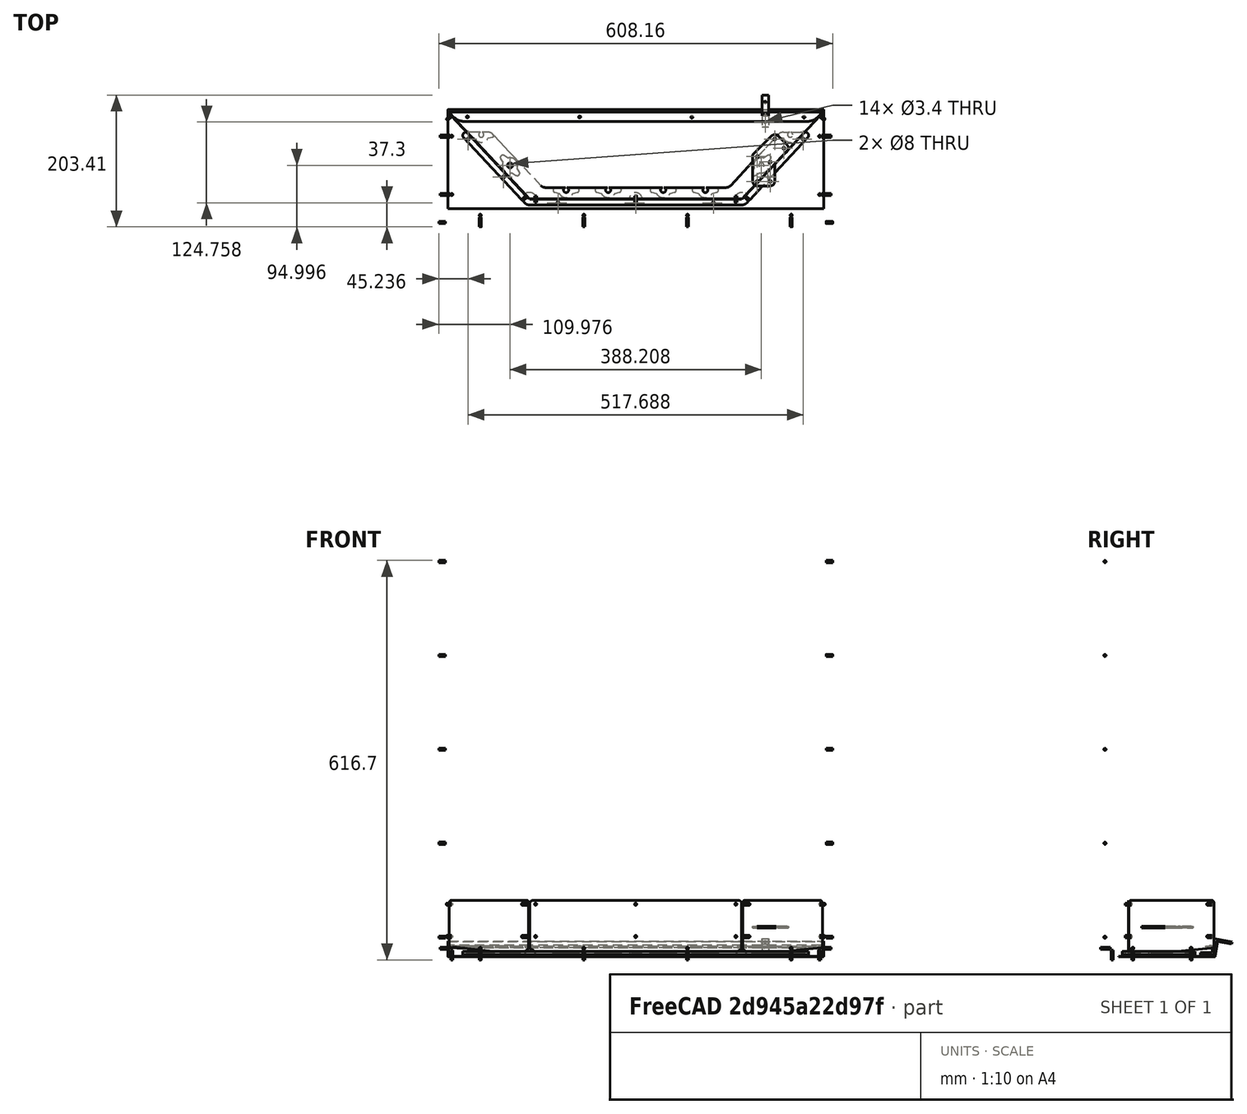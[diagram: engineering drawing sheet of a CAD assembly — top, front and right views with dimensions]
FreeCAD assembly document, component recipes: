
FREECAD ASSEMBLY — COMPONENT RECIPES ("composit_stand5")

This assembly document has 19 components, labeled P0..P18 below (a component is one placed body or linked part). 18 of them carry a construction recipe — the FreeCAD feature program that regenerates the part from scratch, quoted from this document or its linked companion documents; the rest are supplied as boundary geometry only. No exploded tour is included for this assembly.
NOTE — document 2 of 2 of this assembly tour. The two overview renders and the header above are repeated from document 1; the component sections below continue where the previous document stopped.
COMPONENT P18 — recipe-attached ("top", modeled in this document).
Construction recipe (the document's own serialized feature program — sketch geometry with constraints, then the solid features built on it; lengths are millimeters unless a unit is written):

FEATURE [PartDesign::SubShapeBinder] Binder006
  BindCopyOnChange = 0
  BindMode = 0
  ClaimChildren = true
  Context = -> Body002 [Binder006.]
  Fuse = false
  MakeFace = true
  OffsetFill = false
  OffsetIntersection = false
  OffsetJoinType = 0
  OffsetOpenResult = false
  PartialLoad = false
  Relative = false
  Support = -> [Compound006]
  _Version = 2
FEATURE [PartDesign::Pad] Pad
  Direction = (0,0,1)
  Length = 5
  Length2 = 10
  Profile = -> Binder006
  Type = 0
FEATURE [PartDesign::SubShapeBinder] Binder007
  BindCopyOnChange = 0
  BindMode = 0
  ClaimChildren = true
  Context = -> Body002 [Binder007.]
  Fuse = false
  MakeFace = true
  OffsetFill = false
  OffsetIntersection = false
  OffsetJoinType = 0
  OffsetOpenResult = false
  PartialLoad = false
  Relative = false
  Support = -> [Populate008]
  _Version = 2
FEATURE [PartDesign::Pocket] Pocket005
  BaseFeature = -> Pad
  Direction = (0,0,-1)
  Length = 2.5
  Length2 = 5
  Profile = -> Binder007
  Reversed = true
  Type = 0
FEATURE [PartDesign::SubShapeBinder] Binder008
  BindCopyOnChange = 0
  BindMode = 0
  ClaimChildren = true
  Context = -> Body002 [Binder008.]
  Fuse = false
  MakeFace = true
  OffsetFill = false
  OffsetIntersection = false
  OffsetJoinType = 0
  OffsetOpenResult = false
  PartialLoad = false
  Relative = false
  Support = -> [Populate010]
  _Version = 2
FEATURE [PartDesign::Pocket] Pocket006
  BaseFeature = -> Pocket005
  Direction = (0,0,-1)
  Length = 5
  Length2 = 5
  Midplane = true
  Profile = -> Binder008
  Type = 1
FEATURE [PartDesign::SubShapeBinder] Binder010
  BindCopyOnChange = 0
  BindMode = 0
  ClaimChildren = true
  Context = -> Body003 [Binder010.]
  Fuse = false
  MakeFace = true
  OffsetFill = false
  OffsetIntersection = false
  OffsetJoinType = 0
  OffsetOpenResult = false
  PartialLoad = false
  Relative = false
  Support = -> [Populate009]
  _Version = 2
FEATURE [PartDesign::SubShapeBinder] Binder012
  BindCopyOnChange = 0
  BindMode = 0
  ClaimChildren = true
  Context = -> Part002 [Body003.Binder012.]
  Fuse = false
  MakeFace = true
  OffsetFill = false
  OffsetIntersection = false
  OffsetJoinType = 0
  OffsetOpenResult = false
  PartialLoad = false
  Relative = true
  Support = -> [Body[Pocket008.Sketch013.]]
  _Version = 2
FEATURE [PartDesign::SubShapeBinder] Binder013
  BindCopyOnChange = 0
  BindMode = 0
  ClaimChildren = false
  Context = -> Part002 [Body002.Binder013.]
  Fuse = false
  MakeFace = true
  OffsetFill = false
  OffsetIntersection = false
  OffsetJoinType = 0
  OffsetOpenResult = false
  PartialLoad = false
  Relative = true
  Support = -> [Body[Pocket008.Sketch013.]]
  _Version = 2
FEATURE [PartDesign::Pocket] Pocket010
  BaseFeature = -> Pocket006
  Direction = (0,0,-1)
  Length = 5
  Length2 = 5
  Midplane = true
  Profile = -> Binder013
  Type = 1
FEATURE [Sketcher::SketchObject] Sketch027
  FullyConstrained = true
  MapMode = 5
  Support = -> [XY_Plane003]
FEATURE [Sketcher::SketchObject] Sketch029
  FullyConstrained = true
  MapMode = 5
  Placement = pos=(0,0,0) rot=(1,0,0;1.5708rad)
  Support = -> [XZ_Plane003]
FEATURE [PartDesign::SubShapeBinder] Binder022
  BindCopyOnChange = 0
  BindMode = 0
  ClaimChildren = true
  Fuse = false
  MakeFace = true
  OffsetFill = false
  OffsetIntersection = false
  OffsetJoinType = 0
  OffsetOpenResult = false
  PartialLoad = false
  Relative = false
  Support = -> [Populate013]
  _Version = 2
FEATURE [PartDesign::Pocket] Pocket030
  BaseFeature = -> Pocket010
  Direction = (0,0,-1)
  Length = 1
  Length2 = 5
  Profile = -> Binder022
  Reversed = true
  Type = 0
FEATURE [PartDesign::Body] Body002  label="droppers_top_fix"
  Group = -> [Binder006,Pad,Binder007,Pocket005,Binder008,Pocket006,Binder013,Pocket010,Binder022,Pocket030]
  Origin = -> Origin002
  Placement = pos=(0,0,3) rot=(0,0,1;0rad)
  Tip = -> Pocket030
FEATURE [Sketcher::SketchObject] Sketch043
  AttachmentOffset = pos=(0,0,290) rot=(0,0,1;0rad)
  FullyConstrained = true
  MapMode = 5
  Placement = pos=(290,0,0) rot=(0.57735,0.57735,0.57735;2.0944rad)
  Support = -> [YZ_Plane003]
  expr: Constraints[10] = <<main_sketch>>.Constraints.length
  sketch-geometry (5):
    g0: LineSegment StartX=124.058 StartY=0 StartZ=0 EndX=164.058 EndY=0 EndZ=0
    g1: LineSegment StartX=164.058 StartY=0 StartZ=0 EndX=164.058 EndY=30 EndZ=0
    g2: LineSegment StartX=164.058 StartY=30 StartZ=0 EndX=124.058 EndY=30 EndZ=0
    g3: LineSegment StartX=124.058 StartY=30 StartZ=0 EndX=124.058 EndY=0 EndZ=0
    g4: GeomPoint X=134.058 Y=0 Z=0
  constraints (14):
    c: Coincident(g0,g1)
    c: Coincident(g1,g2)
    c: Coincident(g2,g3)
    c: Coincident(g3,g0)
    c: Horizontal(g0)
    c: Horizontal(g2)
    c: Vertical(g1)
    c: Vertical(g3)
    c: PointOnObject(g0,g-1)
    c: PointOnObject(g4,g-1)
    c: DistanceX(g4) = 134.058
    c: DistanceX(g0,g4) = 10
    c: DistanceY(g0,g2) = 30
    c: DistanceX(g0,g0) = 40
FEATURE [PartDesign::SubShapeBinder] Binder023
  BindCopyOnChange = 0
  BindMode = 0
  ClaimChildren = false
  Context = -> Part002 [Body012.Binder023.]
  Fuse = false
  MakeFace = true
  OffsetFill = false
  OffsetIntersection = false
  OffsetJoinType = 0
  OffsetOpenResult = false
  PartialLoad = false
  Relative = true
  Support = -> [Body003[Pocket021.Sketch026.]]
  _Version = 2
FEATURE [Sketcher::SketchObject] Sketch044
  ExternalGeometry = -> [Binder023]
  FullyConstrained = true
  MapMode = 5
  Support = -> [XY_Plane015]
  sketch-geometry (5):
    g0: LineSegment StartX=175.913 StartY=-11.05 StartZ=0 EndX=289.858 EndY=110.695 EndZ=0
    g1: LineSegment StartX=289.858 StartY=110.695 StartZ=0 EndX=297.084 EndY=110.695 EndZ=0
    g2: LineSegment StartX=297.084 StartY=110.695 StartZ=0 EndX=297.084 EndY=-11.05 EndZ=0
    g3: LineSegment StartX=175.913 StartY=-11.05 StartZ=0 EndX=297.084 EndY=-11.05 EndZ=0
    g4: LineSegment StartX=289.858 StartY=110.695 StartZ=0 EndX=289.274 EndY=111.242 EndZ=0
  constraints (14):
    c: Coincident(g1,g0)
    c: Horizontal(g1)
    c: Coincident(g2,g1)
    c: Vertical(g2)
    c: Coincident(g3,g0)
    c: Coincident(g3,g2)
    c: Horizontal(g3)
    c: Coincident(g4,g0)
    c: Coincident(g4,g-3)
    c: Perpendicular(g-3,g4)
    c: Perpendicular(g0,g4)
    c: Distance(g4) = 0.8
    c: Horizontal(g-3,g0)
    c: Distance(g1,g-4) = 3
FEATURE [PartDesign::FeaturePython] BaseBend007  # WARN: FeaturePython — macro-defined, semantics opaque (R4)
  BendSide = 0
  BendSketch = -> Sketch044
  MidPlane = false
  Reverse = false
  length = 100
  radius = 0.1
  thickness = 0.3
  expr: radius = composit_properties#<<Properties>>.bend_r
  expr: thickness = composit_properties#<<Properties>>.al_thickness
FEATURE [PartDesign::FeaturePython] Bend  # WARN: FeaturePython — macro-defined, semantics opaque (R4)
  AutoMiter = true
  BaseFeature = -> BaseBend007
  BendType = 0
  LengthList = [20]
  LengthSpec = 0
  ReliefFactor = 0.7
  UseReliefFactor = false
  angle = 90
  baseObject = -> BaseBend007 [Edge3]
  bendAList = [90]
  extend1 = 0
  extend2 = 0
  gap1 = 0
  gap2 = 0
  invert = false
  kfactor = 0.5
  length = 20
  maxExtendDist = 5
  minGap = 0.1
  minReliefGap = 1
  miterangle1 = 0
  miterangle2 = 0
  offset = 0
  radius = 0.1
  reliefType = 0
  reliefd = 1
  reliefw = 0.8
  sketchflip = false
  sketchinvert = false
  unfold = false
  expr: radius = BaseBend.radius
FEATURE [PartDesign::SubShapeBinder] Binder024
  BindCopyOnChange = 0
  BindMode = 0
  ClaimChildren = true
  Context = -> Part002 [Body012.Binder024.]
  Fuse = false
  MakeFace = true
  OffsetFill = false
  OffsetIntersection = false
  OffsetJoinType = 0
  OffsetOpenResult = false
  PartialLoad = false
  Relative = true
  Support = -> [Body003[Pocket031.Sketch045.]]
  _Version = 2
FEATURE [PartDesign::Pocket] Pocket032
  BaseFeature = -> Bend
  Direction = (-0.730107,0.683333,-2.3e-15)
  Length = 5
  Length2 = 5
  Profile = -> Binder024
  Reversed = true
  Type = 0
FEATURE [PartDesign::SubShapeBinder] Binder025
  BindCopyOnChange = 0
  BindMode = 0
  ClaimChildren = false
  Context = -> Part002 [Body012.Binder025.]
  Fuse = false
  MakeFace = true
  OffsetFill = false
  OffsetIntersection = false
  OffsetJoinType = 0
  OffsetOpenResult = false
  PartialLoad = false
  Relative = true
  Support = -> [Body[Sketch013.]]
  _Version = 2
FEATURE [PartDesign::Pocket] Pocket033
  BaseFeature = -> Pocket032
  Direction = (0,0,-1)
  Length = 5
  Length2 = 5
  Midplane = true
  Profile = -> Binder025
  Type = 1
FEATURE [PartDesign::Body] Body012  label="top_corner_material_0.30ansi"
  Group = -> [Binder023,Sketch044,BaseBend007,Bend,Binder024,Pocket032,Binder025,Pocket033]
  Origin = -> Origin015
  Tip = -> Pocket033
FEATURE [PartDesign::SubShapeBinder] Binder041
  BindCopyOnChange = 0
  BindMode = 0
  ClaimChildren = false
  Context = -> Part002 [Body014.Binder041.]
  Fuse = false
  MakeFace = true
  OffsetFill = false
  OffsetIntersection = false
  OffsetJoinType = 0
  OffsetOpenResult = false
  PartialLoad = false
  Relative = true
  Support = -> [Body003[BaseBend002.Sketch011.]]
  _Version = 2
FEATURE [Sketcher::SketchObject] Sketch074
  ExternalGeometry = -> [Binder041]
  FullyConstrained = true
  MapMode = 5
  Placement = pos=(0,0,0) rot=(0.57735,0.57735,0.57735;2.0944rad)
  Support = -> [YZ_Plane017]
  sketch-geometry (11):
    g0: LineSegment StartX=135.271 StartY=24.1563 StartZ=0 EndX=159.891 EndY=19.8151 EndZ=0
    g1: LineSegment StartX=159.891 StartY=19.8151 StartZ=0 EndX=160.412 EndY=22.7695 EndZ=0
    g2: LineSegment StartX=160.412 StartY=22.7695 StartZ=0 EndX=132.838 EndY=27.6317 EndZ=0
    g3: LineSegment StartX=132.838 StartY=27.6317 StartZ=0 EndX=129.023 EndY=6 EndZ=0
    g4: LineSegment StartX=129.023 StartY=6 StartZ=0 EndX=111.541 EndY=6 EndZ=0
    g5: LineSegment StartX=111.541 StartY=6 StartZ=0 EndX=111.541 EndY=3 EndZ=0
    g6: LineSegment StartX=135.271 StartY=24.1563 StartZ=0 EndX=131.541 EndY=3 EndZ=0
    g7: LineSegment StartX=131.541 StartY=3 StartZ=0 EndX=111.541 EndY=3 EndZ=0
    g8: LineSegment StartX=131.541 StartY=0 StartZ=0 EndX=131.541 EndY=3 EndZ=0
    g9: LineSegment StartX=131.541 StartY=3 StartZ=0 EndX=134.495 EndY=2.47906 EndZ=0
    g10: LineSegment StartX=135.271 StartY=24.1563 StartZ=0 EndX=132.317 EndY=24.6773 EndZ=0
  constraints (33):
    c: Coincident(g0,g1)
    c: Coincident(g1,g2)
    c: Coincident(g2,g3)
    c: Coincident(g3,g4)
    c: Horizontal(g4)
    c: Coincident(g4,g5)
    c: Vertical(g5)
    c: Coincident(g0,g6)
    c: Coincident(g6,g7)
    c: Coincident(g7,g5)
    c: Parallel(g7,g-1)
    c: Parallel(g6,g-3)
    c: Perpendicular(g6,g0)
    c: Perpendicular(g1,g0)
    c: Perpendicular(g2,g1)
    c: Perpendicular(g3,g2)
    c: PointOnObject(g-3,g0)
    c: PointOnObject(g8,g-1)
    c: Coincident(g8,g6)
    c: Vertical(g8)
    c: Coincident(g8,g9)
    c: PointOnObject(g9,g-3)
    c: Perpendicular(g9,g-3)
    c: Equal(g9,g8)
    c: Distance(g8) = 3
    c: Coincident(g10,g0)
    c: PointOnObject(g10,g3)
    c: Perpendicular(g3,g10)
    c: Equal(g10,g1)
    c: Equal(g1,g5)
    c: DistanceY(g5,g5) = 3
    c: Distance(g-3,g0) = 22
    c: DistanceX(g7,g7) = 20
FEATURE [PartDesign::Pad] Pad010
  Direction = (1,0,0)
  Length = 10
  Length2 = 10
  Midplane = true
  Placement = pos=(0,0,0) rot=(0.57735,0.57735,0.57735;2.0944rad)
  Profile = -> Sketch074
  ReferenceAxis = -> Sketch074 [N_Axis]
  Type = 0
FEATURE [PartDesign::SubShapeBinder] Binder042
  BindCopyOnChange = 0
  BindMode = 0
  ClaimChildren = false
  Context = -> Part002 [Body003.Binder042.]
  Fuse = false
  MakeFace = true
  OffsetFill = false
  OffsetIntersection = false
  OffsetJoinType = 0
  OffsetOpenResult = false
  PartialLoad = false
  Placement = pos=(0,0,0) rot=(0.57735,0.57735,0.57735;2.0944rad)
  Relative = false
  Support = -> [Sketch011]
  _Version = 2
  expr: Support = <<top_BaseSketch>>._self
FEATURE [PartDesign::FeaturePython] BaseBend002  label="top_BaseBend"  # WARN: FeaturePython — macro-defined, semantics opaque (R4)
  BendSide = 0
  BendSketch = -> Binder042
  MidPlane = true
  Reverse = false
  length = 580.168
  radius = 0.1
  thickness = 0.3
  expr: length = <<main_sketch>>.Constraints.outer_width
FEATURE [PartDesign::Pocket] Pocket021
  BaseFeature = -> BaseBend002
  Direction = (0,0,-1)
  Length = 1
  Length2 = 5
  Profile = -> Sketch026
  ReferenceAxis = -> Sketch026 [N_Axis]
  Reversed = true
  Type = 0
FEATURE [PartDesign::Mirrored] Mirrored005
  BaseFeature = -> Pocket021
  MirrorPlane = -> YZ_Plane003
  Originals = -> [Pocket021]
FEATURE [PartDesign::FeaturePython] Bend007  # WARN: FeaturePython — macro-defined, semantics opaque (R4)
  AutoMiter = false
  BaseFeature = -> Mirrored005
  BendType = 0
  LengthList = [20]
  LengthSpec = 0
  ReliefFactor = 0.7
  UseReliefFactor = false
  angle = 90
  baseObject = -> Mirrored005 [Edge2,Edge5,Edge8,Edge11,Edge14,Edge17]
  bendAList = [90]
  extend1 = 0
  extend2 = 0
  gap1 = 0
  gap2 = 0
  invert = false
  kfactor = 0.5
  length = 20
  maxExtendDist = 5
  minGap = 0.1
  minReliefGap = 1
  miterangle1 = 0
  miterangle2 = 0
  offset = 0
  radius = 0.1
  reliefType = 0
  reliefd = 1
  reliefw = 0.8
  sketchflip = false
  sketchinvert = false
  unfold = false
  expr: radius = <<top_BaseBend>>.radius
FEATURE [PartDesign::Pocket] Pocket009
  BaseFeature = -> Bend007
  Direction = (0,0,-1)
  Length = 5
  Length2 = 5
  Midplane = true
  Profile = -> Binder012
  Refine = true
  Type = 1
FEATURE [PartDesign::Pocket] Pocket007
  BaseFeature = -> Pocket009
  Direction = (0,0,-1)
  Length = 5
  Length2 = 5
  Midplane = true
  Profile = -> Binder010
  Type = 1
FEATURE [PartDesign::Pocket] Pocket031
  BaseFeature = -> Pocket007
  Direction = (-0.730107,0.683333,-1e-16)
  Length = 5
  Length2 = 5
  Profile = -> Sketch045
  ReferenceAxis = -> Sketch045 [N_Axis]
  Reversed = true
  Type = 0
FEATURE [PartDesign::Mirrored] Mirrored008
  BaseFeature = -> Pocket031
  MirrorPlane = -> YZ_Plane003
  Originals = -> [Pocket031]
FEATURE [PartDesign::Boolean] Boolean005
  BaseFeature = -> Pad010
  Type = 1
FEATURE [PartDesign::Body] Body014  label="lamp_holder"
  Group = -> [Binder041,Sketch074,Pad010,Boolean005]
  Origin = -> Origin017
  Placement = pos=(200,0,0) rot=(0,0,1;0rad)
  Tip = -> Boolean005
FEATURE [PartDesign::Boolean] Boolean006
  BaseFeature = -> Mirrored008
  Group = -> [Compound012]
  Type = 1
  expr: Group = <<top_cut1>>._self
FEATURE [PartDesign::Body] Body003  label="top_material_0.30ansi"
  Group = -> [BaseBend002,Sketch027,Sketch029,Sketch043,Pocket021,Mirrored005,Bend007,Pocket009,Pocket007,Pocket031,Mirrored008,Boolean006,Binder010,Binder042,Binder012]
  Origin = -> Origin003
  Tip = -> BaseBend002
PROVENANCE & LICENSES
A FreeCAD (.FCStd) document from a public repository crawl; recipes are the document's own serialized feature recipes (and, for linked parts, companion documents' recipes).
License: as declared in the source repository (recorded in the dataset sidecar).
